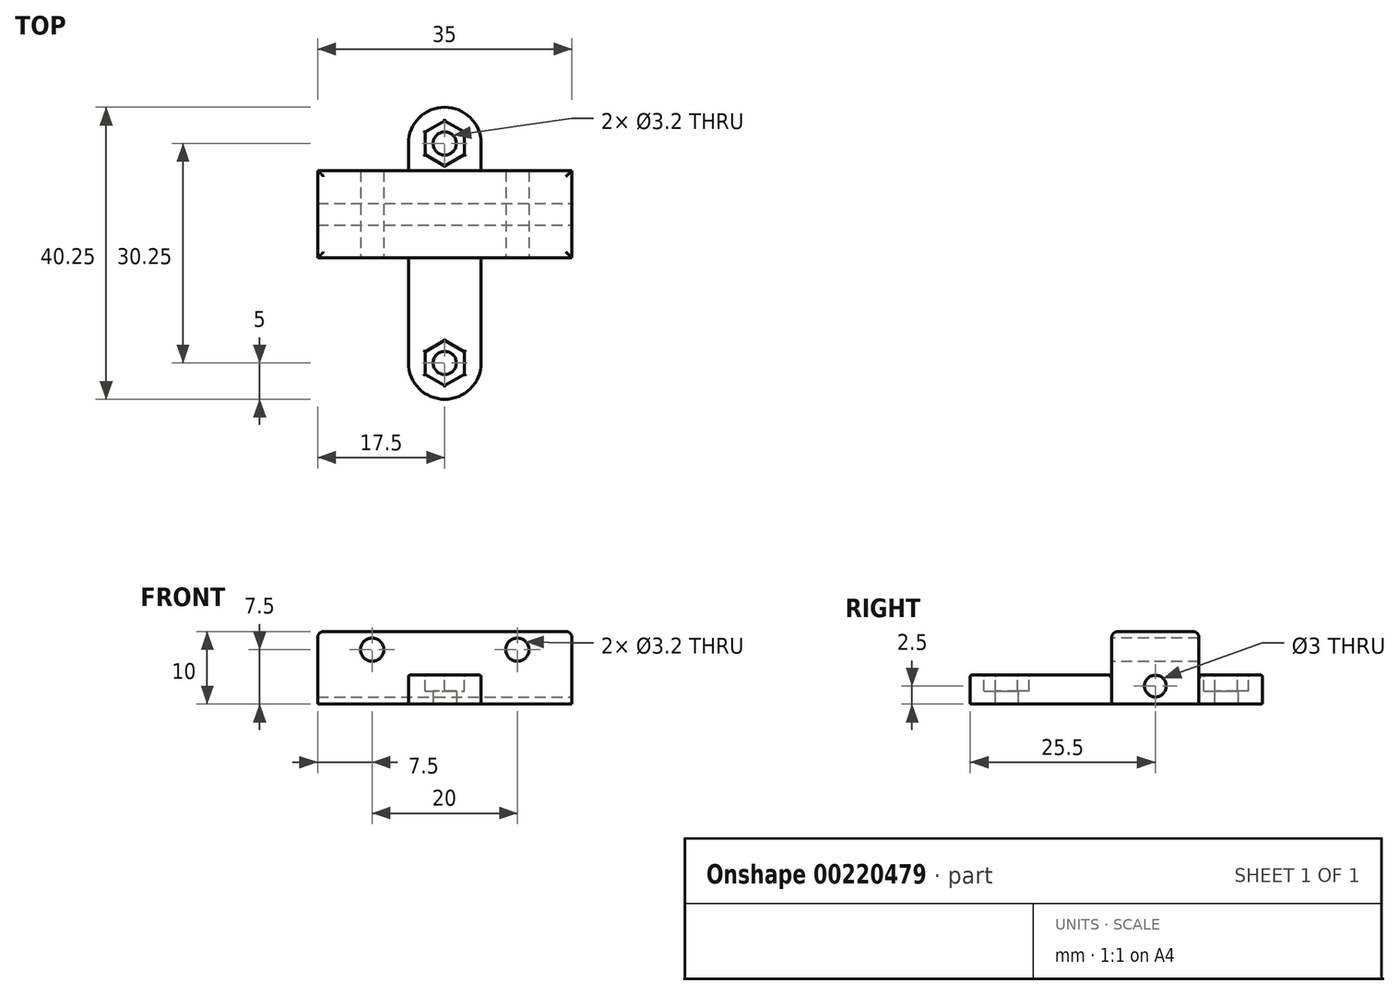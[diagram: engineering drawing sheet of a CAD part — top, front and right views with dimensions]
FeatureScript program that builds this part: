
annotation { "Feature Type Name" : "Feature", "Feature Type Description" : "" }
export const myFeature = defineFeature(function(context is Context, id is Id, definition is map)
    precondition{}
    {
        {
            var Q0;
            Q0=qCreatedBy(makeId("Top.planeOp"),FACE);
            var sketch = newSketch(context, id + "F0", { "sketchPlane" : qUnion([Q0])});
            skCircle(sketch, "E0", {"center": v(0, 30.25) * mm, "radius": 1.6 * mm});
            skCircle(sketch, "E1", {"center": v(0, 0) * mm, "radius": 1.6 * mm});
            skLineSegment(sketch, "E2", {"start": v(0, 30.25) * mm, "end": v(0, 0) * mm, "construction": true});
            skLineSegment(sketch, "E3", {"start": v(-5, 30.25) * mm, "end": v(-5, 26.5) * mm});
            skLineSegment(sketch, "E4", {"start": v(-5, 26.5) * mm, "end": v(-17.5, 26.5) * mm});
            skLineSegment(sketch, "E5", {"start": v(-17.5, 26.5) * mm, "end": v(-17.5, 14.5) * mm});
            skLineSegment(sketch, "E6", {"start": v(-17.5, 14.5) * mm, "end": v(-5, 14.5) * mm});
            skLineSegment(sketch, "E7", {"start": v(-5, 14.5) * mm, "end": v(-5, 0) * mm});
            skLineSegment(sketch, "E8", {"start": v(5, 0) * mm, "end": v(5, 14.5) * mm});
            skLineSegment(sketch, "E9", {"start": v(5, 14.5) * mm, "end": v(17.5, 14.5) * mm});
            skLineSegment(sketch, "E10", {"start": v(17.5, 14.5) * mm, "end": v(17.5, 26.5) * mm});
            skLineSegment(sketch, "E11", {"start": v(17.5, 26.5) * mm, "end": v(5, 26.5) * mm});
            skLineSegment(sketch, "E12", {"start": v(5, 26.5) * mm, "end": v(5, 30.25) * mm});
            skArc(sketch, "E13", {"start": v(-5, 30.25) * mm, "mid": v(0, 35.25) * mm, "end": v(5, 30.25) * mm});
            skArc(sketch, "E14", {"start": v(-5, 0) * mm, "mid": v(0, -5) * mm, "end": v(5, 0) * mm});
            skSolve(sketch);
        }
        {
            var Q0;
            Q0 = qSketchRegion(id + "F0", true);
            extrude(context, id + "F1", {"entities" : qUnion([Q0]), "depth" : 4 * mm});
        }
        {
            var Q0;
            Q0=makeQuery(id+"F1.opExtrude","CAP_FACE",FACE,{"disambiguationData":[OSD([sQuery(id+"F0.wireOp",EDGE,"E0"),sQuery(id+"F0.wireOp",EDGE,"E1"),sQuery(id+"F0.wireOp",EDGE,"E3"),sQuery(id+"F0.wireOp",EDGE,"E4"),sQuery(id+"F0.wireOp",EDGE,"E5"),sQuery(id+"F0.wireOp",EDGE,"E6"),sQuery(id+"F0.wireOp",EDGE,"E7"),sQuery(id+"F0.wireOp",EDGE,"E8"),sQuery(id+"F0.wireOp",EDGE,"E9"),sQuery(id+"F0.wireOp",EDGE,"E10"),sQuery(id+"F0.wireOp",EDGE,"E11"),sQuery(id+"F0.wireOp",EDGE,"E12"),sQuery(id+"F0.wireOp",EDGE,"E13"),sQuery(id+"F0.wireOp",EDGE,"E14")])],"isStart":false});
            var sketch = newSketch(context, id + "F2", { "sketchPlane" : qUnion([Q0])});
            skLineSegment(sketch, "E15.bottom", {"start": v(-17.5, 26.5) * mm, "end": v(17.5, 26.5) * mm});
            skLineSegment(sketch, "E15.top", {"start": v(-17.5, 14.5) * mm, "end": v(17.5, 14.5) * mm});
            skLineSegment(sketch, "E15.left", {"start": v(-17.5, 26.5) * mm, "end": v(-17.5, 14.5) * mm});
            skLineSegment(sketch, "E15.right", {"start": v(17.5, 26.5) * mm, "end": v(17.5, 14.5) * mm});
            skSolve(sketch);
        }
        {
            var Q0;
            Q0 = qSketchRegion(id + "F2", true);
            extrude(context, id + "F3", {"entities" : qUnion([Q0]), "operationType" : NewBodyOperationType.ADD, "depth" : 6 * mm});
        }
        {
            var Q0;
            Q0=makeQuery(id+"F3.boolean.opBoolean","MERGE",FACE,{"derivedFrom":[makeQuery(id+"F1.opExtrude","SWEPT_FACE",FACE,{"disambiguationData":[OSD([sQuery(id+"F0.wireOp",EDGE,"E6")])]}),makeQuery(id+"F1.opExtrude","SWEPT_FACE",FACE,{"disambiguationData":[OSD([sQuery(id+"F0.wireOp",EDGE,"E9")])]}),makeQuery(id+"F3.opExtrude","SWEPT_FACE",FACE,{"disambiguationData":[OSD([sQuery(id+"F2.wireOp",EDGE,"E15.top")])]})]});
            var sketch = newSketch(context, id + "F4", { "sketchPlane" : qUnion([Q0])});
            skCircle(sketch, "E16", {"center": v(-10, 7.5) * mm, "radius": 1.6 * mm});
            skCircle(sketch, "E17", {"center": v(10, 7.5) * mm, "radius": 1.6 * mm});
            skLineSegment(sketch, "E18", {"start": v(-10, 7.5) * mm, "end": v(10, 7.5) * mm, "construction": true});
            skLineSegment(sketch, "E19", {"start": v(0, 10) * mm, "end": v(0, 7.5) * mm, "construction": true});
            skSolve(sketch);
        }
        {
            var Q0;
            Q0 = qSketchRegion(id + "F4", true);
            extrude(context, id + "F5", {"entities" : qUnion([Q0]), "operationType" : NewBodyOperationType.REMOVE, "endBound" : BoundingType.THROUGH_ALL, "oppositeDirection" : true, "depth" : 25 * mm});
        }
        {
            var Q0;
            Q0=makeQuery(id+"F3.opExtrude","CAP_FACE",FACE,{"disambiguationData":[OSD([sQuery(id+"F2.wireOp",EDGE,"E15.bottom"),sQuery(id+"F2.wireOp",EDGE,"E15.top"),sQuery(id+"F2.wireOp",EDGE,"E15.left"),sQuery(id+"F2.wireOp",EDGE,"E15.right")])],"isStart":false});
            fillet(context, id + "F6", {"entities" : qUnion([Q0]), "radius" : 0.8 * mm, "tangentPropagation" : true, "allowEdgeOverflow" : false});
        }
        {
            var Q0;
            Q0=makeQuery(id+"F3.boolean.opBoolean","MERGE",FACE,{"derivedFrom":[makeQuery(id+"F1.opExtrude","SWEPT_FACE",FACE,{"disambiguationData":[OSD([sQuery(id+"F0.wireOp",EDGE,"E10")])]}),makeQuery(id+"F3.opExtrude","SWEPT_FACE",FACE,{"disambiguationData":[OSD([sQuery(id+"F2.wireOp",EDGE,"E15.right")])]})]});
            var sketch = newSketch(context, id + "F7", { "sketchPlane" : qUnion([Q0])});
            skCircle(sketch, "E20", {"center": v(20.5, 2.5) * mm, "radius": 1.5 * mm});
            skPoint(sketch, "E21", {"position": v(20.5, 0) * mm});
            skLineSegment(sketch, "E22", {"start": v(20.5, 0) * mm, "end": v(20.5, 2.5) * mm, "construction": true});
            skSolve(sketch);
        }
        {
            var Q0;
            Q0 = qSketchRegion(id + "F7", true);
            extrude(context, id + "F8", {"entities" : qUnion([Q0]), "operationType" : NewBodyOperationType.REMOVE, "endBound" : BoundingType.THROUGH_ALL, "oppositeDirection" : true, "depth" : 25 * mm});
        }
        {
            var Q0;
            {var subQ0=sQuery(id+"F0.wireOp",EDGE,"E11");var subQ1=sQuery(id+"F0.wireOp",EDGE,"E3");var subQ2=sQuery(id+"F0.wireOp",EDGE,"E4");var subQ3=sQuery(id+"F0.wireOp",EDGE,"E0");var subQ4=sQuery(id+"F0.wireOp",EDGE,"E12");var subQ5=sQuery(id+"F0.wireOp",EDGE,"E13");Q0=makeQuery(id+"F3.boolean.opBoolean","SPLIT",FACE,{"disambiguationData":[TD([makeQuery(id+"F1.opExtrude","SWEPT_FACE",FACE,{"disambiguationData":[OSD([subQ3])]})])],"derivedFrom":makeQuery(id+"F1.opExtrude","CAP_FACE",FACE,{"disambiguationData":[OSD([subQ3,sQuery(id+"F0.wireOp",EDGE,"E1"),subQ1,subQ2,sQuery(id+"F0.wireOp",EDGE,"E5"),sQuery(id+"F0.wireOp",EDGE,"E6"),sQuery(id+"F0.wireOp",EDGE,"E7"),sQuery(id+"F0.wireOp",EDGE,"E8"),sQuery(id+"F0.wireOp",EDGE,"E9"),sQuery(id+"F0.wireOp",EDGE,"E10"),subQ0,subQ4,subQ5,sQuery(id+"F0.wireOp",EDGE,"E14")])],"isStart":false})});}
            var sketch = newSketch(context, id + "F9", { "sketchPlane" : qUnion([Q0])});
            skCircle(sketch, "E23.cCircle", {"center": v(0, 30.25) * mm, "radius": 3.1 * mm, "construction": true});
            skLineSegment(sketch, "E23.0", {"start": v(0, 27.15) * mm, "end": v(-2.68, 28.7) * mm});
            skLineSegment(sketch, "E23.1", {"start": v(-2.68, 28.7) * mm, "end": v(-2.68, 31.8) * mm});
            skLineSegment(sketch, "E23.2", {"start": v(-2.68, 31.8) * mm, "end": v(0, 33.35) * mm});
            skLineSegment(sketch, "E23.3", {"start": v(0, 33.35) * mm, "end": v(2.68, 31.8) * mm});
            skLineSegment(sketch, "E23.4", {"start": v(2.68, 31.8) * mm, "end": v(2.68, 28.7) * mm});
            skLineSegment(sketch, "E23.5", {"start": v(2.68, 28.7) * mm, "end": v(0, 27.15) * mm});
            skCircle(sketch, "E24.cCircle", {"center": v(0, 0) * mm, "radius": 3.1 * mm, "construction": true});
            skLineSegment(sketch, "E24.0", {"start": v(0, 3.1) * mm, "end": v(2.68, 1.55) * mm});
            skLineSegment(sketch, "E24.1", {"start": v(2.68, 1.55) * mm, "end": v(2.68, -1.55) * mm});
            skLineSegment(sketch, "E24.2", {"start": v(2.68, -1.55) * mm, "end": v(0, -3.1) * mm});
            skLineSegment(sketch, "E24.3", {"start": v(0, -3.1) * mm, "end": v(-2.68, -1.55) * mm});
            skLineSegment(sketch, "E24.4", {"start": v(-2.68, -1.55) * mm, "end": v(-2.68, 1.55) * mm});
            skLineSegment(sketch, "E24.5", {"start": v(-2.68, 1.55) * mm, "end": v(0, 3.1) * mm});
            skSolve(sketch);
        }
        {
            var Q0;
            Q0 = qSketchRegion(id + "F9", true);
            extrude(context, id + "F10", {"entities" : qUnion([Q0]), "operationType" : NewBodyOperationType.REMOVE, "oppositeDirection" : true, "depth" : 2.2 * mm});
        }
        {
            var Q0;
            {var subQ0=sQuery(id+"F0.wireOp",EDGE,"E8");var subQ1=sQuery(id+"F0.wireOp",EDGE,"E6");var subQ2=sQuery(id+"F0.wireOp",EDGE,"E7");var subQ3=sQuery(id+"F0.wireOp",EDGE,"E1");var subQ4=sQuery(id+"F0.wireOp",EDGE,"E9");var subQ5=sQuery(id+"F0.wireOp",EDGE,"E14");Q0=makeQuery(id+"F3.boolean.opBoolean","SPLIT",FACE,{"disambiguationData":[TD([makeQuery(id+"F1.opExtrude","SWEPT_FACE",FACE,{"disambiguationData":[OSD([subQ3])]})])],"derivedFrom":makeQuery(id+"F1.opExtrude","CAP_FACE",FACE,{"disambiguationData":[OSD([sQuery(id+"F0.wireOp",EDGE,"E0"),subQ3,sQuery(id+"F0.wireOp",EDGE,"E3"),sQuery(id+"F0.wireOp",EDGE,"E4"),sQuery(id+"F0.wireOp",EDGE,"E5"),subQ1,subQ2,subQ0,subQ4,sQuery(id+"F0.wireOp",EDGE,"E10"),sQuery(id+"F0.wireOp",EDGE,"E11"),sQuery(id+"F0.wireOp",EDGE,"E12"),sQuery(id+"F0.wireOp",EDGE,"E13"),subQ5])],"isStart":false})});}
            var Q1;
            {var subQ0=sQuery(id+"F0.wireOp",EDGE,"E11");var subQ1=sQuery(id+"F0.wireOp",EDGE,"E3");var subQ2=sQuery(id+"F0.wireOp",EDGE,"E4");var subQ3=sQuery(id+"F0.wireOp",EDGE,"E0");var subQ4=sQuery(id+"F0.wireOp",EDGE,"E12");var subQ5=sQuery(id+"F0.wireOp",EDGE,"E13");Q1=makeQuery(id+"F3.boolean.opBoolean","SPLIT",FACE,{"disambiguationData":[TD([makeQuery(id+"F1.opExtrude","SWEPT_FACE",FACE,{"disambiguationData":[OSD([subQ3])]})])],"derivedFrom":makeQuery(id+"F1.opExtrude","CAP_FACE",FACE,{"disambiguationData":[OSD([subQ3,sQuery(id+"F0.wireOp",EDGE,"E1"),subQ1,subQ2,sQuery(id+"F0.wireOp",EDGE,"E5"),sQuery(id+"F0.wireOp",EDGE,"E6"),sQuery(id+"F0.wireOp",EDGE,"E7"),sQuery(id+"F0.wireOp",EDGE,"E8"),sQuery(id+"F0.wireOp",EDGE,"E9"),sQuery(id+"F0.wireOp",EDGE,"E10"),subQ0,subQ4,subQ5,sQuery(id+"F0.wireOp",EDGE,"E14")])],"isStart":false})});}
            var Q2;
            Q2=makeQuery(id+"F1.opExtrude","SWEPT_FACE",FACE,{"disambiguationData":[OSD([sQuery(id+"F0.wireOp",EDGE,"E3")])]});
            fillet(context, id + "F11", {"entities" : qUnion([Q0, Q1, Q2]), "radius" : 0.2 * mm, "tangentPropagation" : true, "allowEdgeOverflow" : false});
        }
    });
